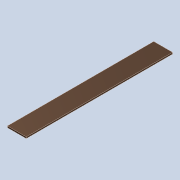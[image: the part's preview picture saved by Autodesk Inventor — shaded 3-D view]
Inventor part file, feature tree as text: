
AUTODESK INVENTOR PART (.ipt)
format: ipt  version: 2021 (Build 250183000, 183)  size: 78,848 bytes
history: native  units: in
note: dims shown in document units (in); Inventor stores cm internally (conversion verified against a paired STEP export)
features: extrude x1, sketch x1
ambient origin geometry x8: Origin, YZ Plane, XZ Plane, XY Plane, X Axis, Y Axis, Z Axis, Center Point
bodies: Solid1 (feature_tree)
feature tree (2):
  extrude  "Extrusion1"  Depth=17.9375in
  sketch  "Sketch1"  dims[d0=2.3125in d1=17.9375in d2=0.1875in d3=0.0in]
